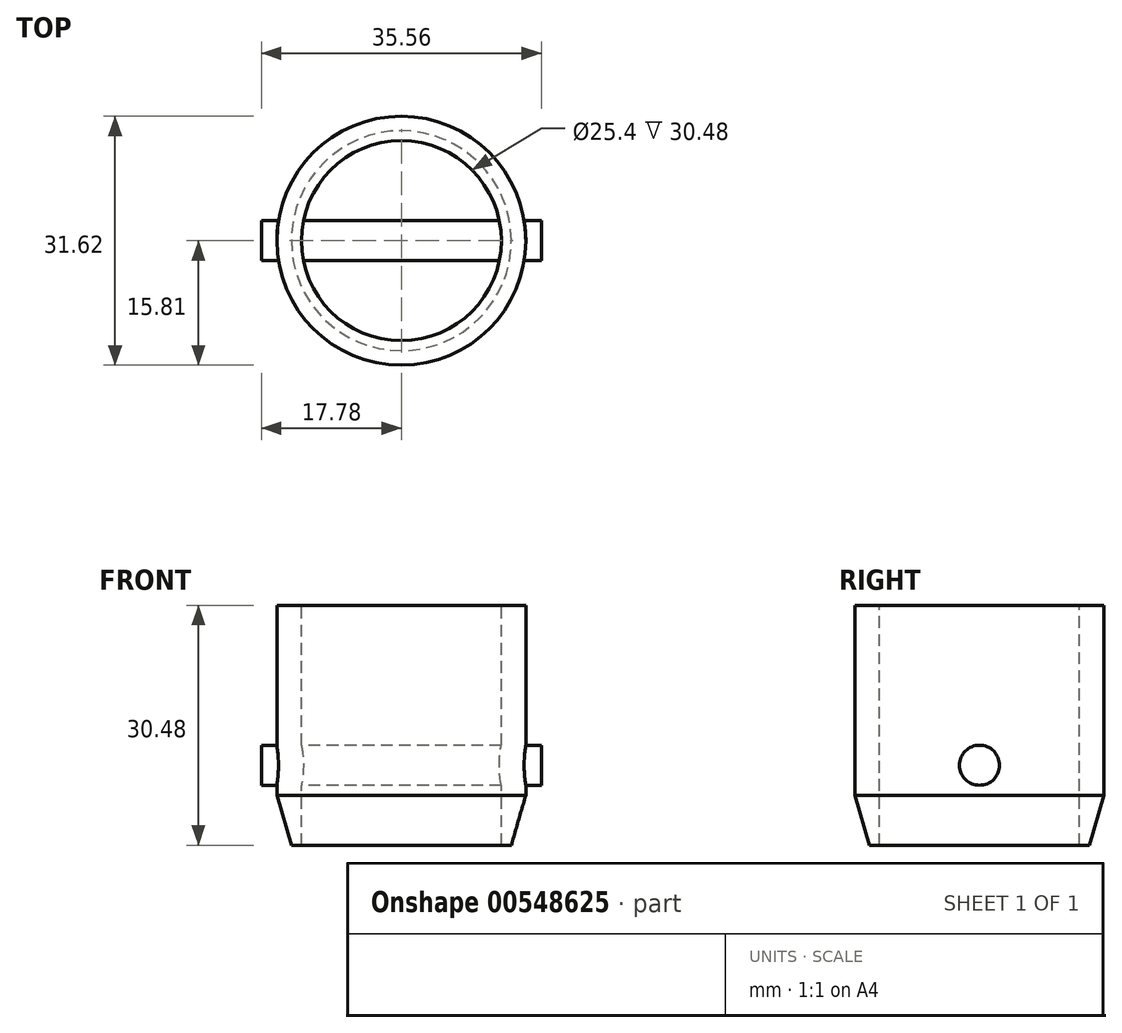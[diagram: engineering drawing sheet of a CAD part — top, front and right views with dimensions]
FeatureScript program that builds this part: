
annotation { "Feature Type Name" : "Feature", "Feature Type Description" : "" }
export const myFeature = defineFeature(function(context is Context, id is Id, definition is map)
    precondition{}
    {
        {
            var Q0;
            Q0=qCreatedBy(makeId("Front.planeOp"),FACE);
            var sketch = newSketch(context, id + "F0", { "sketchPlane" : qUnion([Q0])});
            skLineSegment(sketch, "E0.bottom", {"start": v(13.97, 7.62) * mm, "end": v(12.7, 7.62) * mm});
            skLineSegment(sketch, "E0.top", {"start": v(15.81, 38.1) * mm, "end": v(12.7, 38.1) * mm});
            skLineSegment(sketch, "E0.left", {"start": v(15.81, 13.97) * mm, "end": v(15.81, 38.1) * mm});
            skLineSegment(sketch, "E0.right", {"start": v(12.7, 7.62) * mm, "end": v(12.7, 38.1) * mm});
            skLineSegment(sketch, "E1", {"start": v(15.81, 13.97) * mm, "end": v(13.97, 7.62) * mm});
            skSolve(sketch);
        }
        {
            var Q0;
            Q0=qCreatedBy(makeId("Front.planeOp"),FACE);
            var sketch = newSketch(context, id + "F1", { "sketchPlane" : qUnion([Q0])});
            skLineSegment(sketch, "E2", {"start": v(0, 26.67) * mm, "end": v(0, 0) * mm});
            skSolve(sketch);
        }
        {
            var Q0;
            Q0=makeQuery(id+"F0.imprint","IMPRINT",FACE,{"disambiguationData":[TD([[makeQuery(id+"F0.imprint","IMPRINT",EDGE,{"derivedFrom":sQuery(id+"F0.wireOp",EDGE,"E0.bottom")}),-1.0]])]});
            var Q1;
            Q1=sQuery(id+"F1.wireOp",EDGE,"E2");
            revolve(context, id + "F2", {"entities" : qUnion([Q0]), "axis" : qUnion([Q1]), "revolveType" : RevolveType.FULL});
        }
        {
            var Q0;
            Q0=qCreatedBy(makeId("Right.planeOp"),FACE);
            var sketch = newSketch(context, id + "F3", { "sketchPlane" : qUnion([Q0])});
            skCircle(sketch, "E3", {"center": v(0, 17.78) * mm, "radius": 2.54 * mm});
            skSolve(sketch);
        }
        {
            var Q0;
            Q0=makeQuery(id+"F3.imprint","IMPRINT",FACE,{"disambiguationData":[TD([[makeQuery(id+"F3.imprint","IMPRINT",EDGE,{"derivedFrom":sQuery(id+"F3.wireOp",EDGE,"E3")}),1.0]])]});
            extrude(context, id + "F4", {"entities" : qUnion([Q0]), "operationType" : NewBodyOperationType.ADD, "endBound" : BoundingType.SYMMETRIC, "depth" : 35.56 * mm, "offsetDistance" : 25.4 * mm});
        }
    });
